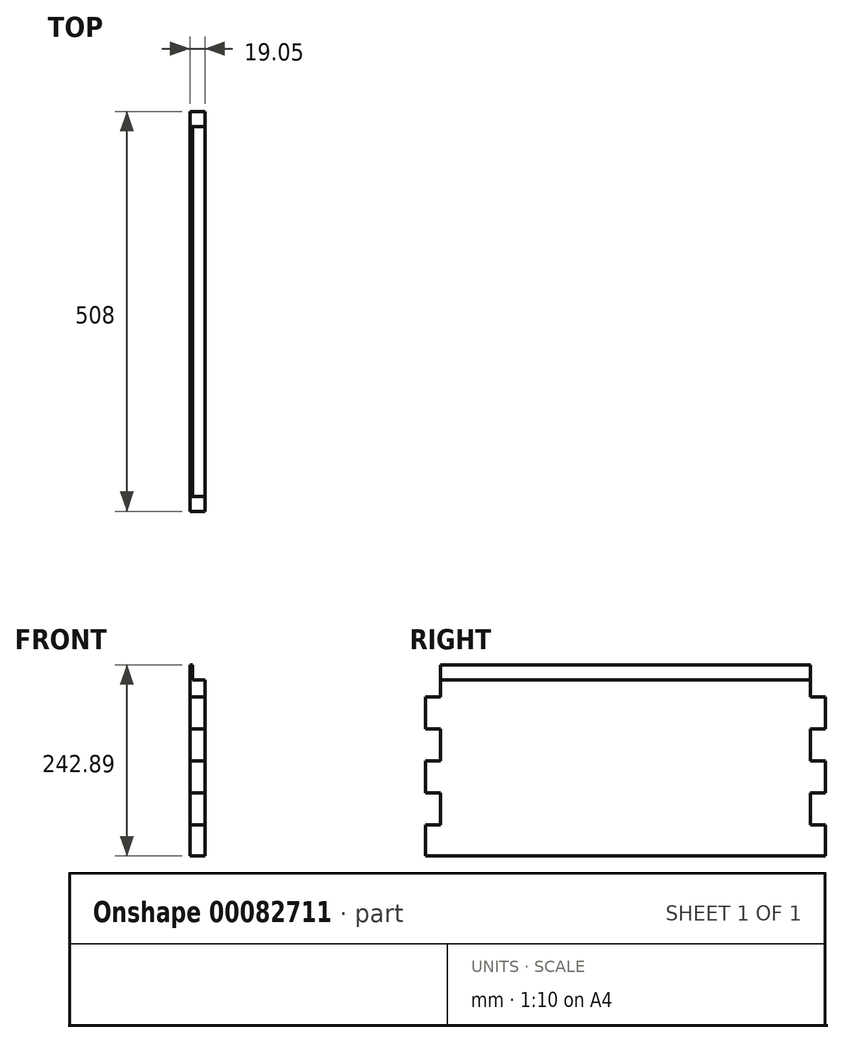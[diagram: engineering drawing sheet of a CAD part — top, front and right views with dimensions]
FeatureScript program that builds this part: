
annotation { "Feature Type Name" : "Feature", "Feature Type Description" : "" }
export const myFeature = defineFeature(function(context is Context, id is Id, definition is map)
    precondition{}
    {
        {
            var Q0;
            Q0=qCreatedBy(makeId("Right.planeOp"),FACE);
            var sketch = newSketch(context, id + "F0", { "sketchPlane" : qUnion([Q0])});
            skLineSegment(sketch, "E0.top", {"start": v(-618.08, -133.37) * mm, "end": v(-599.03, -133.37) * mm});
            skLineSegment(sketch, "E0.right", {"start": v(-599.03, -92.73) * mm, "end": v(-599.03, -133.37) * mm});
            skLineSegment(sketch, "E1.top", {"start": v(-618.08, -174.01) * mm, "end": v(-599.03, -174.01) * mm});
            skLineSegment(sketch, "E1.left", {"start": v(-618.08, -133.37) * mm, "end": v(-618.08, -174.01) * mm});
            skLineSegment(sketch, "E2.top", {"start": v(-618.08, -214.65) * mm, "end": v(-599.03, -214.65) * mm});
            skLineSegment(sketch, "E2.right", {"start": v(-599.03, -174.01) * mm, "end": v(-599.03, -214.65) * mm});
            skLineSegment(sketch, "E3.top", {"start": v(-618.08, -255.3) * mm, "end": v(-599.03, -255.3) * mm});
            skLineSegment(sketch, "E3.left", {"start": v(-618.08, -214.65) * mm, "end": v(-618.08, -255.3) * mm});
            skLineSegment(sketch, "E4.top", {"start": v(-618.08, -295.93) * mm, "end": v(-599.03, -295.93) * mm});
            skLineSegment(sketch, "E4.right", {"start": v(-599.03, -255.3) * mm, "end": v(-599.03, -295.93) * mm});
            skLineSegment(sketch, "E5.top", {"start": v(-618.08, -335.62) * mm, "end": v(-599.03, -335.62) * mm});
            skLineSegment(sketch, "E5.left", {"start": v(-618.08, -295.93) * mm, "end": v(-618.08, -335.62) * mm});
            skLineSegment(sketch, "E6", {"start": v(-364.08, -92.73) * mm, "end": v(-364.08, -335.62) * mm, "construction": true});
            skLineSegment(sketch, "E7.MirrorCS", {"start": v(-110.08, -295.93) * mm, "end": v(-129.13, -295.93) * mm});
            skLineSegment(sketch, "E8.MirrorCS", {"start": v(-110.08, -174.01) * mm, "end": v(-129.13, -174.01) * mm});
            skLineSegment(sketch, "E9.MirrorCS", {"start": v(-110.08, -133.37) * mm, "end": v(-129.13, -133.37) * mm});
            skLineSegment(sketch, "E10.MirrorCS", {"start": v(-110.08, -214.65) * mm, "end": v(-129.13, -214.65) * mm});
            skLineSegment(sketch, "E11.MirrorCS", {"start": v(-110.08, -255.3) * mm, "end": v(-129.13, -255.3) * mm});
            skLineSegment(sketch, "E12.MirrorCS", {"start": v(-110.08, -295.93) * mm, "end": v(-110.08, -335.62) * mm});
            skLineSegment(sketch, "E13.MirrorCS", {"start": v(-110.08, -335.62) * mm, "end": v(-129.13, -335.62) * mm});
            skLineSegment(sketch, "E14.MirrorCS", {"start": v(-110.08, -214.65) * mm, "end": v(-110.08, -255.3) * mm});
            skLineSegment(sketch, "E15.MirrorCS", {"start": v(-110.08, -133.37) * mm, "end": v(-110.08, -174.01) * mm});
            skLineSegment(sketch, "E16.MirrorCS", {"start": v(-129.13, -255.3) * mm, "end": v(-129.13, -295.93) * mm});
            skLineSegment(sketch, "E17.MirrorCS", {"start": v(-129.13, -174.01) * mm, "end": v(-129.13, -214.65) * mm});
            skLineSegment(sketch, "E18.MirrorCS", {"start": v(-129.13, -92.73) * mm, "end": v(-129.13, -133.37) * mm});
            skLineSegment(sketch, "E19", {"start": v(-129.13, -92.73) * mm, "end": v(-599.03, -92.73) * mm});
            skLineSegment(sketch, "E20", {"start": v(-129.13, -335.62) * mm, "end": v(-599.03, -335.62) * mm});
            skSolve(sketch);
        }
        {
            var Q0;
            Q0=makeQuery(id+"F0.imprint","IMPRINT",FACE,{"disambiguationData":[TD([[makeQuery(id+"F0.imprint","IMPRINT",EDGE,{"derivedFrom":sQuery(id+"F0.wireOp",EDGE,"E0.right")}),1.0]])]});
            extrude(context, id + "F1", {"entities" : qUnion([Q0]), "depth" : 19.05 * mm});
        }
        {
            var Q0;
            Q0=makeQuery(id+"F1.opExtrude","CAP_FACE",FACE,{"disambiguationData":[OSD([sQuery(id+"F0.wireOp",EDGE,"E0.right"),sQuery(id+"F0.wireOp",EDGE,"E0.top"),sQuery(id+"F0.wireOp",EDGE,"E1.left"),sQuery(id+"F0.wireOp",EDGE,"E1.top"),sQuery(id+"F0.wireOp",EDGE,"E2.right"),sQuery(id+"F0.wireOp",EDGE,"E2.top"),sQuery(id+"F0.wireOp",EDGE,"E3.left"),sQuery(id+"F0.wireOp",EDGE,"E3.top"),sQuery(id+"F0.wireOp",EDGE,"E4.right"),sQuery(id+"F0.wireOp",EDGE,"E4.top"),sQuery(id+"F0.wireOp",EDGE,"E5.top"),sQuery(id+"F0.wireOp",EDGE,"E5.left"),sQuery(id+"F0.wireOp",EDGE,"E12.MirrorCS"),sQuery(id+"F0.wireOp",EDGE,"E13.MirrorCS"),sQuery(id+"F0.wireOp",EDGE,"E14.MirrorCS"),sQuery(id+"F0.wireOp",EDGE,"E7.MirrorCS"),sQuery(id+"F0.wireOp",EDGE,"E8.MirrorCS"),sQuery(id+"F0.wireOp",EDGE,"E9.MirrorCS"),sQuery(id+"F0.wireOp",EDGE,"E15.MirrorCS"),sQuery(id+"F0.wireOp",EDGE,"E11.MirrorCS"),sQuery(id+"F0.wireOp",EDGE,"E10.MirrorCS"),sQuery(id+"F0.wireOp",EDGE,"E16.MirrorCS"),sQuery(id+"F0.wireOp",EDGE,"E17.MirrorCS"),sQuery(id+"F0.wireOp",EDGE,"E18.MirrorCS"),sQuery(id+"F0.wireOp",EDGE,"E19"),sQuery(id+"F0.wireOp",EDGE,"E20")])],"isStart":false});
            var sketch = newSketch(context, id + "F2", { "sketchPlane" : qUnion([Q0])});
            skLineSegment(sketch, "E21", {"start": v(-599.03, -92.73) * mm, "end": v(-599.03, -111.78) * mm});
            skLineSegment(sketch, "E22", {"start": v(-599.03, -111.78) * mm, "end": v(-129.13, -111.78) * mm});
            skLineSegment(sketch, "E23", {"start": v(-129.13, -111.78) * mm, "end": v(-129.13, -92.73) * mm});
            skLineSegment(sketch, "E24", {"start": v(-129.13, -92.73) * mm, "end": v(-599.03, -92.73) * mm});
            skSolve(sketch);
        }
        {
            var Q0;
            Q0=qSketchRegion(id+"F2",true);
            extrude(context, id + "F3", {"entities" : qUnion([Q0]), "operationType" : NewBodyOperationType.REMOVE, "oppositeDirection" : true, "depth" : 15.88 * mm});
        }
    });
